# Revit family: Cabinet-Teknion-CEBS_Base_Cabinet_Door(s)-R2023
name_source: partatom
category: Furniture
units: mm (PartAtom-declared; Revit-internal decimal feet)

## family parameters
Always vertical = Yes
Cut with Voids When Loaded = No
Enable Cutting in Views = No
OmniClass Number = 23.40.20.00
OmniClass Title = General Furniture and Specialties
Render Appearance Source = Family Geometry
Room Calculation Point = No
Shared = Yes
Work Plane-Based = No

## types (4) — shared parameters
Assembly Code = E2020200
Manufacturer = Teknion
Manufacturer Fax = 416.661.4586
Part Number = CEBS
Product Documentation Link = https://www.teknion.com
Product Line = Base Cabinets
Product Page URL = https://www.teknion.com
Series = Expansion Casework+
Sustainability Data = https://www.teknion.com
URL = www.teknion.com
Unit Weight URL = http://www.teknion.com
Warranty = http://www.teknion.com
zero-valued in all types: Default Elevation

## per-type parameters (varying)
| type | Actual Depth | Description | Height | Model |
| 29D,35H | 30.024 " | Base Cabinet – Door(s), 29D,35H | 35 " | CEBS29__35 |
| 29D,32H | 30.024 " | Base Cabinet – Door(s), 29D,32H | 32 " | CEBS29__32 |
| 24D,35H | 25.024 " | Base Cabinet – Door(s), 24D,35H | 35 " | CEBS24__35 |
| 24D,32H | 25.024 " | Base Cabinet – Door(s), 24D,32H | 32 " | CEBS24__32 |

## geometry (parser evidence)
native form markers: Sweep x2
no freeform markers — native parametric forms only
